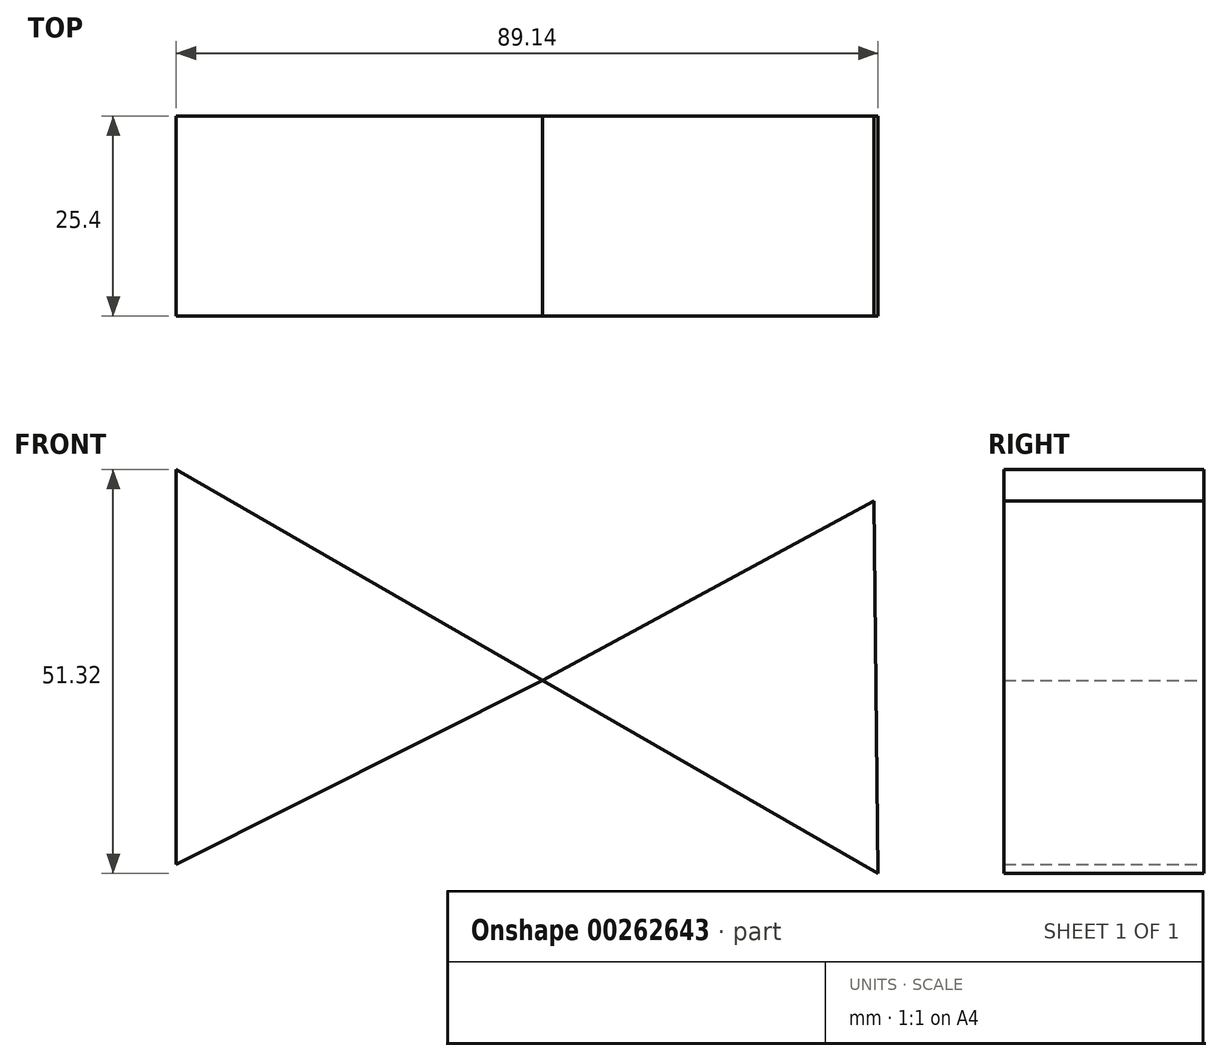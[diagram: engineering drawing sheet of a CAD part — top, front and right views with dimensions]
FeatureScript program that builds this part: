
annotation { "Feature Type Name" : "Feature", "Feature Type Description" : "" }
export const myFeature = defineFeature(function(context is Context, id is Id, definition is map)
    precondition{}
    {
        {
            var Q0;
            Q0=qCreatedBy(makeId("Front.planeOp"),FACE);
            var sketch = newSketch(context, id + "F0", { "sketchPlane" : qUnion([Q0])});
            skLineSegment(sketch, "E0", {"start": v(-46.53, 50.17) * mm, "end": v(-46.53, 0) * mm});
            skLineSegment(sketch, "E1", {"start": v(-46.53, 50.17) * mm, "end": v(0, 23.38) * mm});
            skLineSegment(sketch, "E2", {"start": v(-46.53, 0) * mm, "end": v(0, 23.38) * mm});
            skLineSegment(sketch, "E3", {"start": v(0, 23.38) * mm, "end": v(42.06, 46.17) * mm});
            skLineSegment(sketch, "E4", {"start": v(0, 23.38) * mm, "end": v(42.61, -1.15) * mm});
            skLineSegment(sketch, "E5", {"start": v(42.61, -1.15) * mm, "end": v(42.06, 46.17) * mm});
            skSolve(sketch);
        }
        {
            var Q0;
            Q0 = qSketchRegion(id + "F0", true);
            extrude(context, id + "F1", {"entities" : qUnion([Q0]), "depth" : 25.4 * mm});
        }
    });
